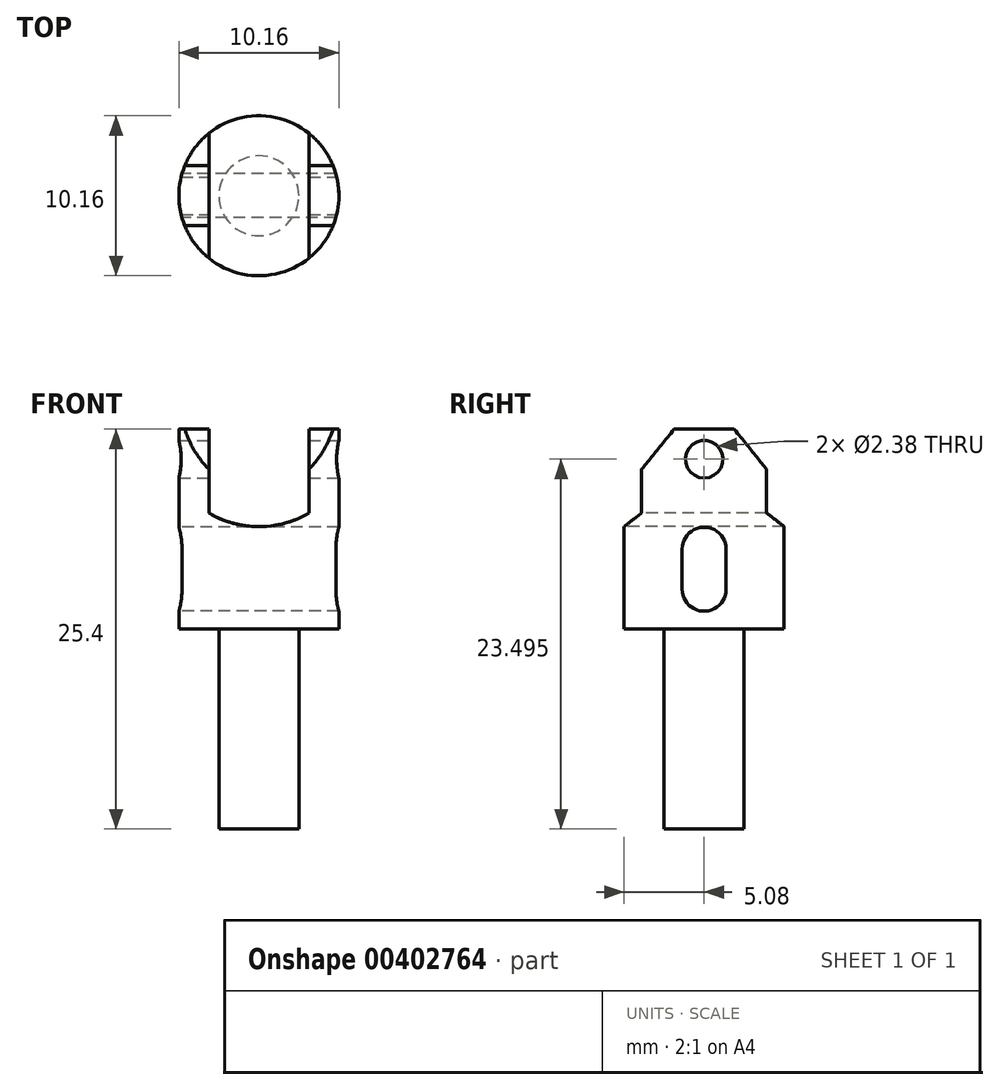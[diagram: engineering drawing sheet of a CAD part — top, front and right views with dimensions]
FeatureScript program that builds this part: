
annotation { "Feature Type Name" : "Feature", "Feature Type Description" : "" }
export const myFeature = defineFeature(function(context is Context, id is Id, definition is map)
    precondition{}
    {
        {
            var Q0;
            Q0=qCreatedBy(makeId("Top.planeOp"),FACE);
            var sketch = newSketch(context, id + "F0", { "sketchPlane" : qUnion([Q0])});
            skCircle(sketch, "E0", {"center": v(0, 0) * mm, "radius": 5.08 * mm});
            skSolve(sketch);
        }
        {
            var Q0;
            Q0=makeQuery(id+"F0.imprint","IMPRINT",FACE,{"disambiguationData":[TD([[makeQuery(id+"F0.imprint","IMPRINT",EDGE,{"derivedFrom":sQuery(id+"F0.wireOp",EDGE,"E0")}),1.0]])]});
            extrude(context, id + "F1", {"entities" : qUnion([Q0]), "depth" : 12.7 * mm});
        }
        {
            var Q0;
            Q0=makeQuery(id+"F1.opExtrude","CAP_FACE",FACE,{"disambiguationData":[OSD([sQuery(id+"F0.wireOp",EDGE,"E0")])],"isStart":true});
            var sketch = newSketch(context, id + "F2", { "sketchPlane" : qUnion([Q0])});
            skCircle(sketch, "E1", {"center": v(0, 0) * mm, "radius": 2.54 * mm});
            skSolve(sketch);
        }
        {
            var Q0;
            Q0=makeQuery(id+"F2.imprint","IMPRINT",FACE,{"disambiguationData":[TD([[makeQuery(id+"F2.imprint","IMPRINT",EDGE,{"derivedFrom":sQuery(id+"F2.wireOp",EDGE,"E1")}),1.0]])]});
            var Q1;
            Q1=sQuery(id+"F2.wireOp",EDGE,"E1");
            extrude(context, id + "F3", {"entities" : qUnion([Q0]), "operationType" : NewBodyOperationType.ADD, "surfaceEntities" : qUnion([Q1]), "depth" : 12.7 * mm});
        }
        {
            var Q0;
            Q0=qCreatedBy(makeId("Front.planeOp"),FACE);
            var sketch = newSketch(context, id + "F4", { "sketchPlane" : qUnion([Q0])});
            skLineSegment(sketch, "E2.bottom", {"start": v(-3.18, 12.7) * mm, "end": v(3.18, 12.7) * mm});
            skLineSegment(sketch, "E2.top", {"start": v(-3.18, 7.62) * mm, "end": v(3.18, 7.62) * mm});
            skLineSegment(sketch, "E2.left", {"start": v(-3.18, 12.7) * mm, "end": v(-3.18, 7.62) * mm});
            skLineSegment(sketch, "E2.right", {"start": v(3.17, 12.7) * mm, "end": v(3.17, 7.62) * mm});
            skLineSegment(sketch, "E3", {"start": v(0, 0) * mm, "end": v(0, 12.7) * mm, "construction": true});
            skSolve(sketch);
        }
        {
            var Q0;
            Q0 = qSketchRegion(id + "F4", true);
            extrude(context, id + "F5", {"entities" : qUnion([Q0]), "operationType" : NewBodyOperationType.REMOVE, "endBound" : BoundingType.SYMMETRIC, "oppositeDirection" : true, "depth" : 25.4 * mm});
        }
        {
            var Q0;
            Q0=qCreatedBy(makeId("Right.planeOp"),FACE);
            var sketch = newSketch(context, id + "F6", { "sketchPlane" : qUnion([Q0])});
            skLineSegment(sketch, "E4", {"start": v(0, 0) * mm, "end": v(0, 12.7) * mm, "construction": true});
            skArc(sketch, "E5", {"start": v(-1.4, 5.08) * mm, "mid": v(0, 6.48) * mm, "end": v(1.4, 5.08) * mm});
            skArc(sketch, "E6", {"start": v(1.4, 2.54) * mm, "mid": v(0, 1.14) * mm, "end": v(-1.4, 2.54) * mm});
            skLineSegment(sketch, "E7", {"start": v(-1.4, 5.08) * mm, "end": v(-1.4, 2.54) * mm});
            skLineSegment(sketch, "E8", {"start": v(1.4, 5.08) * mm, "end": v(1.4, 2.54) * mm});
            skSolve(sketch);
        }
        {
            var Q0;
            Q0 = qSketchRegion(id + "F6", true);
            extrude(context, id + "F7", {"entities" : qUnion([Q0]), "operationType" : NewBodyOperationType.REMOVE, "endBound" : BoundingType.THROUGH_ALL, "depth" : 25.4 * mm, "hasSecondDirection" : true, "secondDirectionBound" : SecondDirectionBoundingType.THROUGH_ALL, "secondDirectionOppositeDirection" : true, "secondDirectionDepth" : 25.4 * mm});
        }
        {
            var Q0;
            Q0=qCreatedBy(makeId("Right.planeOp"),FACE);
            var sketch = newSketch(context, id + "F8", { "sketchPlane" : qUnion([Q0])});
            skLineSegment(sketch, "E9", {"start": v(0, 0) * mm, "end": v(0, 12.7) * mm, "construction": true});
            skCircle(sketch, "E10", {"center": v(0, 10.8) * mm, "radius": 1.2 * mm});
            skSolve(sketch);
        }
        {
            var Q0;
            Q0 = qSketchRegion(id + "F8", true);
            var Q1;
            Q1=sQuery(id+"F8.wireOp",EDGE,"E9");
            extrude(context, id + "F9", {"entities" : qUnion([Q0]), "operationType" : NewBodyOperationType.REMOVE, "surfaceEntities" : qUnion([Q1]), "endBound" : BoundingType.THROUGH_ALL, "oppositeDirection" : true, "depth" : 25.4 * mm, "hasSecondDirection" : true, "secondDirectionBound" : SecondDirectionBoundingType.THROUGH_ALL, "secondDirectionOppositeDirection" : false, "secondDirectionDepth" : 25.4 * mm});
        }
        {
            var Q0;
            Q0=makeQuery(id+"F5.boolean.opBoolean","COPY",FACE,{"derivedFrom":makeQuery(id+"F5.opExtrude","SWEPT_FACE",FACE,{"disambiguationData":[OSD([sQuery(id+"F4.wireOp",EDGE,"E2.right")])]})});
            var sketch = newSketch(context, id + "F10", { "sketchPlane" : qUnion([Q0])});
            skLineSegment(sketch, "E11", {"start": v(3.97, 12.7) * mm, "end": v(1.9, 12.7) * mm});
            skLineSegment(sketch, "E12", {"start": v(1.9, 12.7) * mm, "end": v(3.97, 10.16) * mm});
            skLineSegment(sketch, "E13", {"start": v(3.97, 10.16) * mm, "end": v(3.97, 12.7) * mm});
            skLineSegment(sketch, "E14", {"start": v(0, 12.7) * mm, "end": v(0, 0) * mm, "construction": true});
            skLineSegment(sketch, "E15", {"start": v(-1.9, 12.7) * mm, "end": v(-3.97, 10.16) * mm});
            skLineSegment(sketch, "E16", {"start": v(-3.97, 10.16) * mm, "end": v(-3.97, 12.7) * mm});
            skLineSegment(sketch, "E17", {"start": v(-3.97, 12.7) * mm, "end": v(-1.9, 12.7) * mm});
            skSolve(sketch);
        }
        {
            var Q0;
            Q0 = qSketchRegion(id + "F10", true);
            extrude(context, id + "F11", {"entities" : qUnion([Q0]), "operationType" : NewBodyOperationType.REMOVE, "endBound" : BoundingType.SYMMETRIC, "oppositeDirection" : true, "depth" : 25.4 * mm});
        }
        {
            var Q0;
            Q0=qCreatedBy(makeId("Front.planeOp"),FACE);
            var sketch = newSketch(context, id + "F12", { "sketchPlane" : qUnion([Q0])});
            skLineSegment(sketch, "E18", {"start": v(0, 0) * mm, "end": v(0, 12.7) * mm, "construction": true});
            skLineSegment(sketch, "E19.0", {"start": v(3.18, 7.62) * mm, "end": v(-3.18, 7.62) * mm});
            skLineSegment(sketch, "E20", {"start": v(-3.18, 7.62) * mm, "end": v(-3.18, 7.37) * mm});
            skLineSegment(sketch, "E21", {"start": v(3.18, 7.62) * mm, "end": v(3.18, 7.37) * mm});
            skArc(sketch, "E22", {"start": v(-3.18, 7.37) * mm, "mid": v(0, 6.52) * mm, "end": v(3.18, 7.37) * mm});
            skSolve(sketch);
        }
        {
            var Q0;
            Q0 = qSketchRegion(id + "F12", true);
            extrude(context, id + "F13", {"entities" : qUnion([Q0]), "operationType" : NewBodyOperationType.REMOVE, "endBound" : BoundingType.SYMMETRIC, "oppositeDirection" : true, "depth" : 25.4 * mm, "offsetDistance" : 25.4 * mm});
        }
    });
